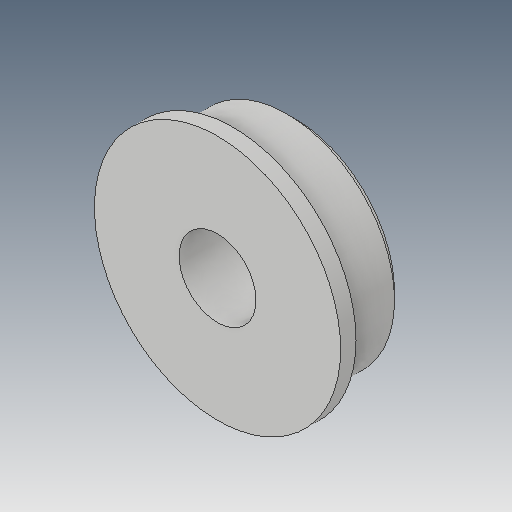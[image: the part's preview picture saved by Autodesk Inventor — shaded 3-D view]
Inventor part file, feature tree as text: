
AUTODESK INVENTOR PART (.ipt)
format: ipt  version: 2017 (Build 210142000, 142)  size: 123,392 bytes
history: native  units: mm
features: other x3, extrude x2, sketch x2, chamfer x1, reference x1
ambient origin geometry x8: Origin, YZ Plane, XZ Plane, XY Plane, X Axis, Y Axis, Z Axis, Center Point
bodies: Solid1 (feature_tree)
feature tree (9):
  extrude  "Extrusion1"  Depth=5.0mm
  extrude  "Extrusion2"  Depth=1.0mm
  chamfer  "Chamfer1"  Distance=1.0mm
  sketch  "Sketch1"  dims[d0=5.0mm d1=14.0mm]
  reference  "Reference1"
  sketch  "Sketch2"  dims[d2=5.0mm d3=0.0mm d4=16.0mm d5=1.0mm d6=0.0mm d7=0.5mm d8=2.0mm d9=45.0deg]
  other  "<userpath>\OneDrive\SL-Inventor\SL-Beast 3D Printer\x-aXIS-aSSEMBLY.iam"
  other  "x-aXIS-aSSEMBLY.iam"
  other  "Washer:1"
